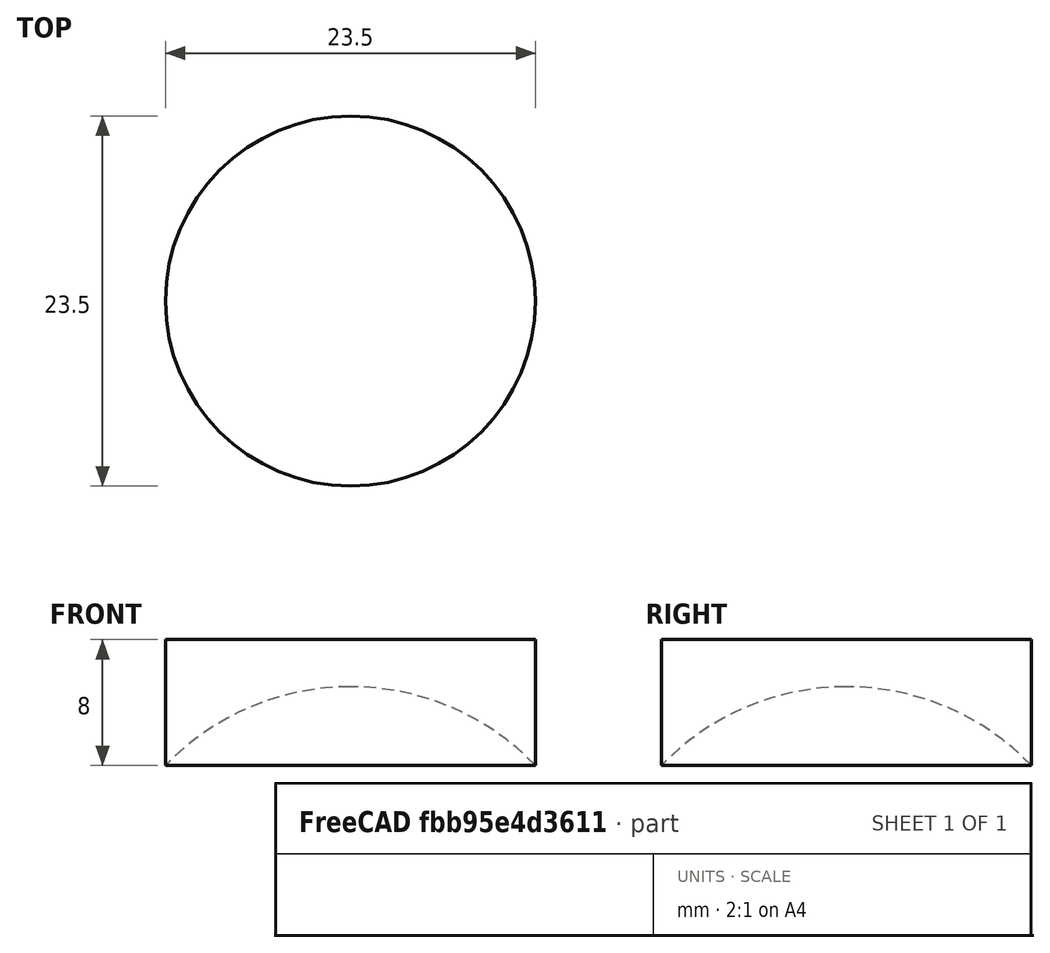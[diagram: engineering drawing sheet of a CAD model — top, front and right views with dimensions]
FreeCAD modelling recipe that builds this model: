
FCSTD DOCUMENT  (FreeCAD 0.18R16146 (Git))
Label: EyePiceLense
License: All rights reserved
LicenseURL: http://en.wikipedia.org/wiki/All_rights_reserved
objects: Sketcher::SketchObject×1, PartDesign::Revolution×1, PartDesign::Body×1
note: 4 computed .brp shape members not serialized (recipe doc carries the construction recipe); baked Part::Feature solids carry a one-line shape summary decoded from their .brp

FEATURE [Sketcher::SketchObject] Sketch
  MapMode = 5
  Placement = pos=(0,0,0) rot=(1,0,0;1.5708rad)
  Support = -> [XZ_Plane]
  sketch-geometry (4):
    g0: LineSegment StartX=1e-15 StartY=8 StartZ=0 EndX=1e-15 EndY=5 EndZ=0
    g1: ArcOfCircle CenterX=0 CenterY=-11.3062 CenterZ=0 NormalX=0 NormalY=0 NormalZ=1 AngleXU=0 Radius=16.3062 StartAngle=0.766154 EndAngle=1.5708
    g2: LineSegment StartX=11.75 StartY=8 StartZ=0 EndX=11.75 EndY=-1.8e-15 EndZ=0
    g3: LineSegment StartX=1e-15 StartY=8 StartZ=0 EndX=11.75 EndY=8 EndZ=0
  constraints (13):
    c: PointOnObject(g0,g-2)
    c: Vertical(g0)
    c: PointOnObject(g1,g-2)
    c: Coincident(g0,g1)
    c: DistanceY(g1,g0) = 8
    c: DistanceX(g0,g2) = 11.75
    c: Vertical(g2)
    c: PointOnObject(g1,g-1)
    c: Coincident(g3,g0)
    c: Coincident(g3,g2)
    c: Horizontal(g3)
    c: Coincident(g2,g1)
    c: DistanceY(g-1,g0) = 5
FEATURE [PartDesign::Revolution] Revolution
  Angle = 360
  Axis = (0,-1.031e-13,1)
  Base = (0,0,0)
  Placement = pos=(0,0,0) rot=(1,0,0;1.5708rad)
  Profile = -> Sketch
  ReferenceAxis = -> Sketch [V_Axis]
  Reversed = true
FEATURE [PartDesign::Body] Body
  Group = -> [Sketch,Revolution]
  Origin = -> Origin
  Tip = -> Revolution
